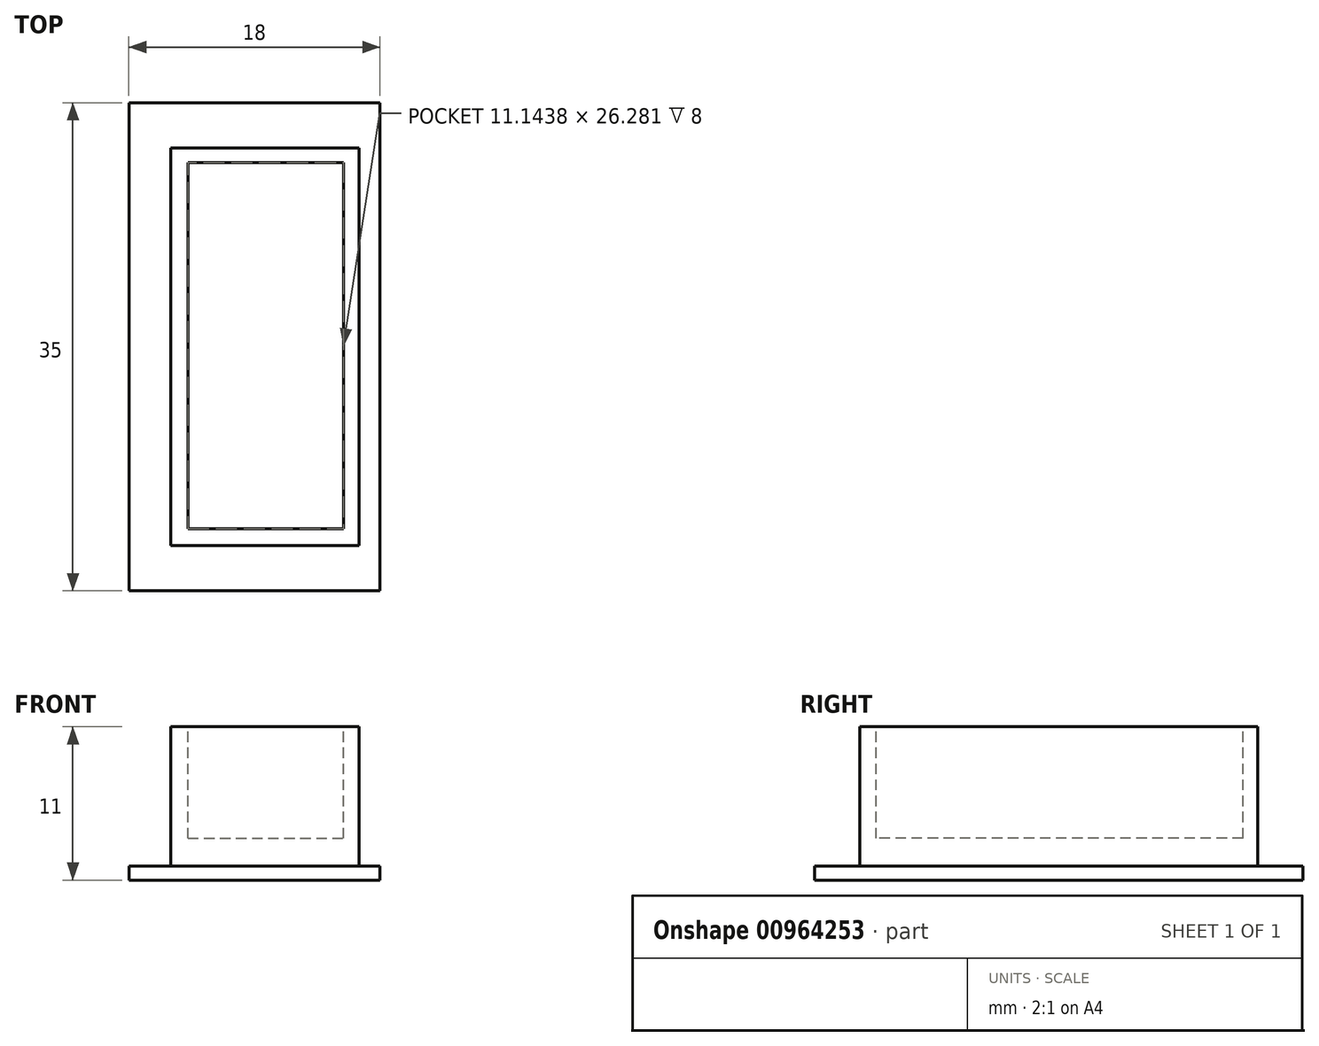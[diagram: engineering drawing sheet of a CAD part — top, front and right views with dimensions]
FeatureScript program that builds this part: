
annotation { "Feature Type Name" : "Feature", "Feature Type Description" : "" }
export const myFeature = defineFeature(function(context is Context, id is Id, definition is map)
    precondition{}
    {
        {
            var Q0;
            Q0=qCreatedBy(makeId("Top.planeOp"),FACE);
            var sketch = newSketch(context, id + "F0", { "sketchPlane" : qUnion([Q0])});
            skLineSegment(sketch, "E0.bottom", {"start": v(-7.98, 17.5) * mm, "end": v(10.02, 17.5) * mm});
            skLineSegment(sketch, "E0.top", {"start": v(-7.98, -17.5) * mm, "end": v(10.02, -17.5) * mm});
            skLineSegment(sketch, "E0.left", {"start": v(-7.98, 17.5) * mm, "end": v(-7.98, -17.5) * mm});
            skLineSegment(sketch, "E0.right", {"start": v(10.02, 17.5) * mm, "end": v(10.02, -17.5) * mm});
            skSolve(sketch);
        }
        {
            var Q0;
            Q0=makeQuery(id+"F0.imprint","IMPRINT",FACE,{"disambiguationData":[TD([[makeQuery(id+"F0.imprint","IMPRINT",EDGE,{"derivedFrom":sQuery(id+"F0.wireOp",EDGE,"E0.bottom")}),-1.0]])]});
            extrude(context, id + "F1", {"entities" : qUnion([Q0]), "depth" : 1 * mm, "offsetDistance" : 25 * mm});
        }
        {
            var Q0;
            Q0=makeQuery(id+"F1.opExtrude","CAP_FACE",FACE,{"disambiguationData":[OSD([sQuery(id+"F0.wireOp",EDGE,"E0.bottom"),sQuery(id+"F0.wireOp",EDGE,"E0.top"),sQuery(id+"F0.wireOp",EDGE,"E0.left"),sQuery(id+"F0.wireOp",EDGE,"E0.right")])],"isStart":false});
            var sketch = newSketch(context, id + "F2", { "sketchPlane" : qUnion([Q0])});
            skLineSegment(sketch, "E1.bottom", {"start": v(-4.98, 14.24) * mm, "end": v(8.52, 14.24) * mm});
            skLineSegment(sketch, "E1.top", {"start": v(-4.98, -14.26) * mm, "end": v(8.52, -14.26) * mm});
            skLineSegment(sketch, "E1.left", {"start": v(-4.98, 14.24) * mm, "end": v(-4.98, -14.26) * mm});
            skLineSegment(sketch, "E1.right", {"start": v(8.52, 14.24) * mm, "end": v(8.52, -14.26) * mm});
            skSolve(sketch);
        }
        {
            var Q0;
            Q0=makeQuery(id+"F2.imprint","IMPRINT",FACE,{"disambiguationData":[TD([[makeQuery(id+"F2.imprint","IMPRINT",EDGE,{"derivedFrom":sQuery(id+"F2.wireOp",EDGE,"E1.bottom")}),-1.0]])]});
            extrude(context, id + "F3", {"entities" : qUnion([Q0]), "operationType" : NewBodyOperationType.ADD, "depth" : 10 * mm, "offsetDistance" : 25 * mm});
        }
        {
            var Q0;
            Q0=makeQuery(id+"F3.opExtrude","CAP_FACE",FACE,{"disambiguationData":[OSD([sQuery(id+"F2.wireOp",EDGE,"E1.bottom"),sQuery(id+"F2.wireOp",EDGE,"E1.top"),sQuery(id+"F2.wireOp",EDGE,"E1.left"),sQuery(id+"F2.wireOp",EDGE,"E1.right")])],"isStart":false});
            var sketch = newSketch(context, id + "F4", { "sketchPlane" : qUnion([Q0])});
            skLineSegment(sketch, "E2.bottom", {"start": v(-3.75, 13.2) * mm, "end": v(7.4, 13.2) * mm});
            skLineSegment(sketch, "E2.top", {"start": v(-3.75, -13.08) * mm, "end": v(7.4, -13.08) * mm});
            skLineSegment(sketch, "E2.left", {"start": v(-3.75, 13.2) * mm, "end": v(-3.75, -13.08) * mm});
            skLineSegment(sketch, "E2.right", {"start": v(7.4, 13.2) * mm, "end": v(7.4, -13.08) * mm});
            skSolve(sketch);
        }
        {
            var Q0;
            Q0=makeQuery(id+"F4.imprint","IMPRINT",FACE,{"disambiguationData":[TD([[makeQuery(id+"F4.imprint","IMPRINT",EDGE,{"derivedFrom":sQuery(id+"F4.wireOp",EDGE,"E2.bottom")}),-1.0]])]});
            extrude(context, id + "F5", {"entities" : qUnion([Q0]), "operationType" : NewBodyOperationType.REMOVE, "oppositeDirection" : true, "depth" : 8 * mm, "offsetDistance" : 25 * mm});
        }
    });
